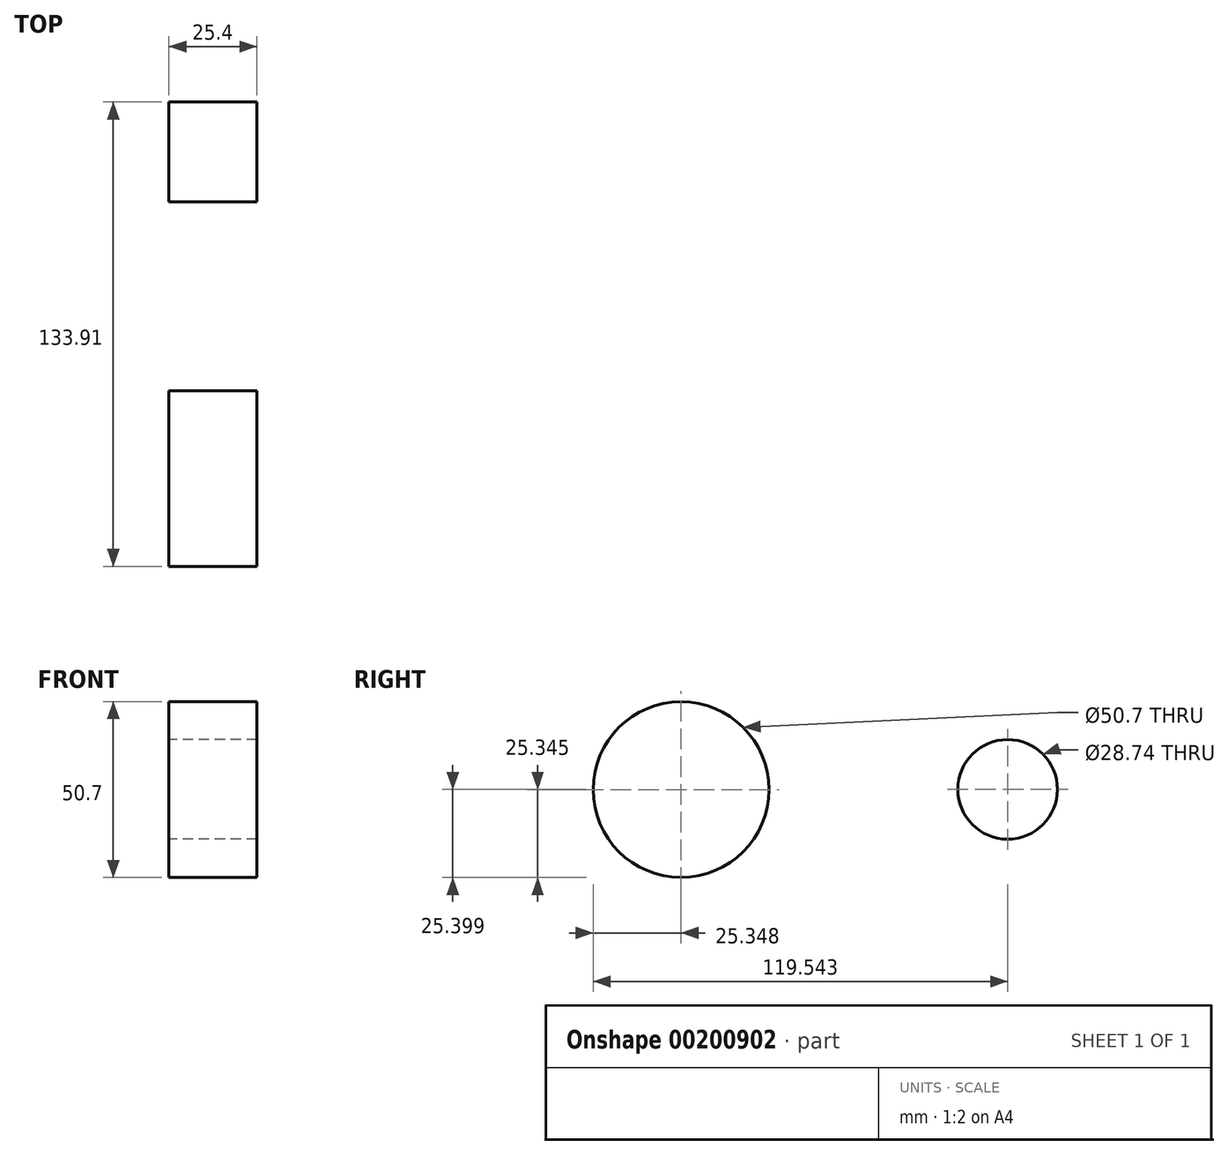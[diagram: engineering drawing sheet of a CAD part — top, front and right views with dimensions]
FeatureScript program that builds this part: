
annotation { "Feature Type Name" : "Feature", "Feature Type Description" : "" }
export const myFeature = defineFeature(function(context is Context, id is Id, definition is map)
    precondition{}
    {
        {
            var Q0;
            Q0=qCreatedBy(makeId("Right.planeOp"),FACE);
            var sketch = newSketch(context, id + "F0", { "sketchPlane" : qUnion([Q0])});
            skCircle(sketch, "E0", {"center": v(-0.15, -0.15) * mm, "radius": 25.35 * mm});
            skCircle(sketch, "E1", {"center": v(94.04, -0.1) * mm, "radius": 14.37 * mm});
            skLineSegment(sketch, "E2", {"start": v(3.04, -25.3) * mm, "end": v(94.04, -14.57) * mm});
            skLineSegment(sketch, "E3", {"start": v(0, 25.35) * mm, "end": v(95.75, 14.17) * mm});
            skSolve(sketch);
        }
        {
            var Q0;
            Q0=sQuery(id+"F0.wireOp",EDGE,"E0");
            var Q1;
            Q1=sQuery(id+"F0.wireOp",EDGE,"E1");
            extrude(context, id + "F1", {"bodyType" : ToolBodyType.SURFACE, "surfaceEntities" : qUnion([Q0, Q1]), "oppositeDirection" : true, "depth" : 25.4 * mm});
        }
    });
